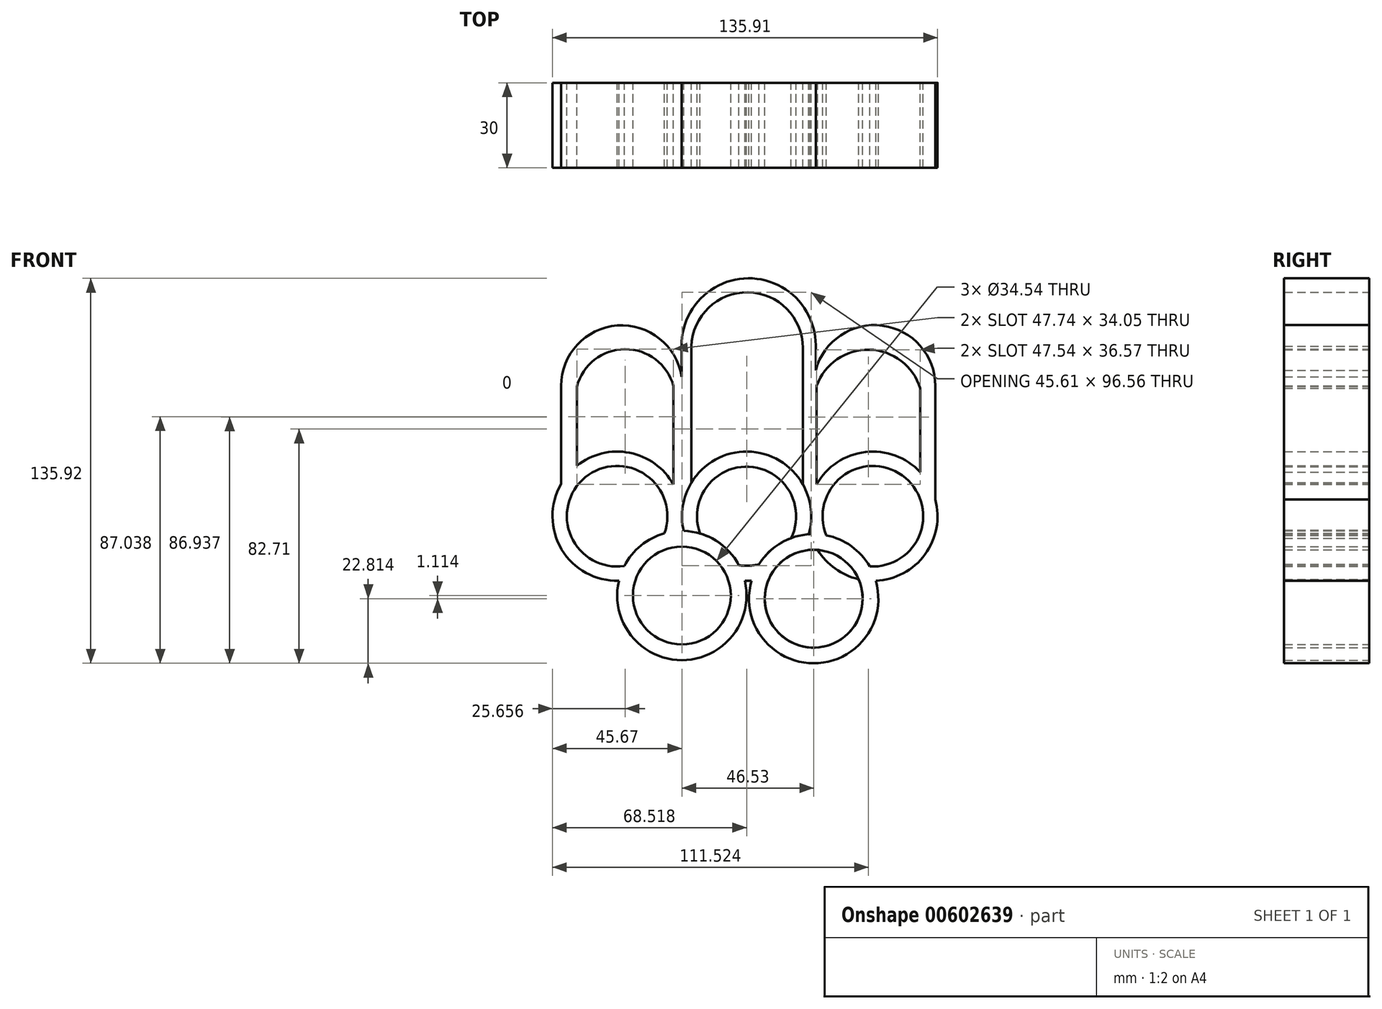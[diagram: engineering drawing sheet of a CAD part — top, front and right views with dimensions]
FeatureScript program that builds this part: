
annotation { "Feature Type Name" : "Feature", "Feature Type Description" : "" }
export const myFeature = defineFeature(function(context is Context, id is Id, definition is map)
    precondition{}
    {
        {
            var Q0;
            Q0=qCreatedBy(makeId("Front.planeOp"),FACE);
            var sketch = newSketch(context, id + "F0", { "sketchPlane" : qUnion([Q0])});
            skPoint(sketch, "E0.center.orphan", {"position": v(-38.59, 0) * mm});
            skArc(sketch, "E1", {"start": v(-45.07, -5.2) * mm, "mid": v(-81.71, 17.68) * mm, "end": v(-66.66, -22.8) * mm});
            skArc(sketch, "E2", {"start": v(0.32, -6.37) * mm, "mid": v(-20.99, 22.8) * mm, "end": v(-43.81, -5.2) * mm});
            skArc(sketch, "E3", {"start": v(3.52, -11.9) * mm, "mid": v(9.68, -18.54) * mm, "end": v(17.94, -22.25) * mm});
            skCircle(sketch, "E4", {"center": v(-44.44, -28) * mm, "radius": 22.82 * mm});
            skCircle(sketch, "E5", {"center": v(2.09, -29.12) * mm, "radius": 22.82 * mm});
            skArc(sketch, "E6", {"start": v(-50.6, -6.03) * mm, "mid": v(-78.5, 13.75) * mm, "end": v(-64.73, -17.56) * mm});
            skArc(sketch, "E7", {"start": v(21.85, -17.71) * mm, "mid": v(33.33, 14.42) * mm, "end": v(6.57, -6.74) * mm});
            skLineSegment(sketch, "E8", {"start": v(-47.43, 11.24) * mm, "end": v(-47.43, 45.98) * mm});
            skLineSegment(sketch, "E9", {"start": v(-41.1, 11.85) * mm, "end": v(-41.1, 60) * mm});
            skLineSegment(sketch, "E10", {"start": v(-1.73, 11.24) * mm, "end": v(-1.73, 59.38) * mm});
            skPoint(sketch, "E11.start.orphan", {"position": v(3.13, 11.24) * mm});
            skLineSegment(sketch, "E12", {"start": v(3.13, 11.24) * mm, "end": v(3.13, 45.98) * mm});
            skLineSegment(sketch, "E13", {"start": v(-87.07, 45.98) * mm, "end": v(-87.07, 11.36) * mm});
            skLineSegment(sketch, "E14", {"start": v(45.03, 45.98) * mm, "end": v(45.03, 5.9) * mm});
            skLineSegment(sketch, "E15", {"start": v(-81.48, 17.87) * mm, "end": v(-81.48, 45.81) * mm});
            skLineSegment(sketch, "E16", {"start": v(39.7, 15.53) * mm, "end": v(39.7, 45.14) * mm});
            skPoint(sketch, "E17.1.internal.orphan", {"position": v(-87.07, 53.58) * mm});
            skPoint(sketch, "E18.1.internal.orphan", {"position": v(-87.07, 49.2) * mm});
            skPoint(sketch, "E18.2.internal.orphan", {"position": v(-83.36, 53.58) * mm});
            skPoint(sketch, "E18.6.internal.orphan", {"position": v(-48.22, 53.58) * mm});
            skArc(sketch, "E19", {"start": v(-44.5, 49.2) * mm, "mid": v(-67.28, 67.33) * mm, "end": v(-87.07, 45.98) * mm});
            skArc(sketch, "E20", {"start": v(-47.43, 45.98) * mm, "mid": v(-64.52, 58.98) * mm, "end": v(-81.48, 45.81) * mm});
            skLineSegment(sketch, "E21", {"start": v(-44.5, 49.2) * mm, "end": v(-44.5, 60) * mm});
            skArc(sketch, "E22", {"start": v(45.03, 45.98) * mm, "mid": v(26.36, 67.28) * mm, "end": v(2.8, 51.56) * mm});
            skArc(sketch, "E23", {"start": v(39.7, 45.14) * mm, "mid": v(21.72, 58.78) * mm, "end": v(3.13, 45.98) * mm});
            skArc(sketch, "E24", {"start": v(-1.73, 59.38) * mm, "mid": v(-21.11, 79.06) * mm, "end": v(-41.1, 60) * mm});
            skLineSegment(sketch, "E25", {"start": v(2.8, 51.56) * mm, "end": v(2.8, 60.34) * mm});
            skArc(sketch, "E26", {"start": v(2.8, 60.34) * mm, "mid": v(-21.03, 84) * mm, "end": v(-44.5, 60) * mm});
            skCircle(sketch, "E27", {"center": v(-44.44, -28) * mm, "radius": 17.27 * mm});
            skCircle(sketch, "E28", {"center": v(2.09, -29.12) * mm, "radius": 17.27 * mm});
            skArc(sketch, "E29", {"start": v(-5.9, -7.74) * mm, "mid": v(-20.7, 17.48) * mm, "end": v(-38, -6.11) * mm});
            skArc(sketch, "E30.trimOffspring", {"start": v(24.01, -22.8) * mm, "mid": v(36.3, 18.54) * mm, "end": v(1.06, -6.32) * mm});
            skArc(sketch, "E31.trimOffspring", {"start": v(-22.22, -22.8) * mm, "mid": v(-21.02, -22.81) * mm, "end": v(-19.82, -22.75) * mm});
            skArc(sketch, "E32.trimOffspring", {"start": v(-24.3, -17.3) * mm, "mid": v(-20.73, -17.48) * mm, "end": v(-17.2, -16.94) * mm});
            skArc(sketch, "E33.trimOffspring", {"start": v(-41.6, -10.97) * mm, "mid": v(-36.02, -17.68) * mm, "end": v(-28.32, -21.8) * mm});
            skArc(sketch, "E34.trimOffspring", {"start": v(-60.56, -21.8) * mm, "mid": v(-52.86, -17.68) * mm, "end": v(-47.28, -10.97) * mm});
            skSolve(sketch);
        }
        {
            var Q0;
            Q0 = qSketchRegion(id + "F0", true);
            var Q1;
            {var subQ0=sQuery(id+"F0.wireOp",EDGE,"E6");var subQ1=sQuery(id+"F0.wireOp",EDGE,"E4");var subQ2=makeQuery(id+"F0.imprint","INTERSECT",VERTEX,{"disambiguationData":[OD(0.0)],"derivedFrom":[subQ1,subQ0]});Q1=makeQuery(id+"F0.imprint","IMPRINT",FACE,{"disambiguationData":[TD([[makeQuery(id+"F0.imprint","IMPRINT",EDGE,{"disambiguationData":[TD([[subQ2,-1.0]])],"derivedFrom":subQ1}),1.0]])]});}
            var Q2;
            {var subQ0=sQuery(id+"F0.wireOp",EDGE,"29F3q1Gk-59Qx-DLio-MAzj-wrFeAYEK7VN9");var subQ1=sQuery(id+"F0.wireOp",EDGE,"E1");var subQ2=makeQuery(id+"F0.imprint","INTERSECT",VERTEX,{"disambiguationData":[OD(0.0)],"derivedFrom":[subQ1,subQ0]});Q2=makeQuery(id+"F0.imprint","IMPRINT",FACE,{"disambiguationData":[TD([[makeQuery(id+"F0.imprint","IMPRINT",EDGE,{"disambiguationData":[TD([[subQ2,-1.0]])],"derivedFrom":subQ1}),1.0]])]});}
            var Q3;
            {var subQ0=sQuery(id+"F0.wireOp",EDGE,"29F3q1Gk-59Qx-DLio-MAzj-wrFeAYEK7VN9");var subQ1=sQuery(id+"F0.wireOp",EDGE,"E1");var subQ2=makeQuery(id+"F0.imprint","INTERSECT",VERTEX,{"disambiguationData":[OD(1.0)],"derivedFrom":[subQ1,subQ0]});Q3=makeQuery(id+"F0.imprint","IMPRINT",FACE,{"disambiguationData":[TD([[makeQuery(id+"F0.imprint","IMPRINT",EDGE,{"disambiguationData":[TD([[subQ2,-1.0]])],"derivedFrom":subQ1}),-1.0]])]});}
            var Q4;
            {var subQ0=sQuery(id+"F0.wireOp",EDGE,"29F3q1Gk-59Qx-DLio-MAzj-wrFeAYEK7VN9");var subQ1=sQuery(id+"F0.wireOp",EDGE,"E2");var subQ2=makeQuery(id+"F0.imprint","INTERSECT",VERTEX,{"disambiguationData":[OD(0.0)],"derivedFrom":[subQ1,subQ0]});Q4=makeQuery(id+"F0.imprint","IMPRINT",FACE,{"disambiguationData":[TD([[makeQuery(id+"F0.imprint","IMPRINT",EDGE,{"disambiguationData":[TD([[subQ2,-1.0]])],"derivedFrom":subQ1}),1.0]])]});}
            var Q5;
            {var subQ0=sQuery(id+"F0.wireOp",EDGE,"qcPD5Bay-Gsfa-sGTU-Rgtn-S3WhtxFdIdAI");var subQ1=sQuery(id+"F0.wireOp",EDGE,"E4");var subQ2=makeQuery(id+"F0.imprint","INTERSECT",VERTEX,{"disambiguationData":[OD(0.0)],"derivedFrom":[subQ1,subQ0]});Q5=makeQuery(id+"F0.imprint","IMPRINT",FACE,{"disambiguationData":[TD([[makeQuery(id+"F0.imprint","IMPRINT",EDGE,{"disambiguationData":[TD([[subQ2,-1.0]])],"derivedFrom":subQ1}),1.0]])]});}
            var Q6;
            {var subQ0=sQuery(id+"F0.wireOp",EDGE,"E2");var subQ4=makeQuery(id+"F0.imprint","INTERSECT",VERTEX,{"derivedFrom":[subQ0,sQuery(id+"F0.wireOp",EDGE,"E10")]});Q6=makeQuery(id+"F0.imprint","IMPRINT",FACE,{"disambiguationData":[TD([[makeQuery(id+"F0.imprint","IMPRINT",EDGE,{"disambiguationData":[TD([[subQ4,1.0]])],"derivedFrom":subQ0}),1.0]])]});}
            var Q7;
            {var subQ0=sQuery(id+"F0.wireOp",EDGE,"JeexFHJX-C1Pv-IVd9-wVUE-wp2mIqmijwAB");var subQ1=sQuery(id+"F0.wireOp",EDGE,"E2");var subQ2=makeQuery(id+"F0.imprint","INTERSECT",VERTEX,{"disambiguationData":[OD(0.0)],"derivedFrom":[subQ1,subQ0]});Q7=makeQuery(id+"F0.imprint","IMPRINT",FACE,{"disambiguationData":[TD([[makeQuery(id+"F0.imprint","IMPRINT",EDGE,{"disambiguationData":[TD([[subQ2,-1.0]])],"derivedFrom":subQ1}),1.0]])]});}
            var Q8;
            {var subQ0=sQuery(id+"F0.wireOp",EDGE,"qcPD5Bay-Gsfa-sGTU-Rgtn-S3WhtxFdIdAI");var subQ1=sQuery(id+"F0.wireOp",EDGE,"E5");var subQ2=makeQuery(id+"F0.imprint","INTERSECT",VERTEX,{"disambiguationData":[OD(0.0)],"derivedFrom":[subQ1,subQ0]});Q8=makeQuery(id+"F0.imprint","IMPRINT",FACE,{"disambiguationData":[TD([[makeQuery(id+"F0.imprint","IMPRINT",EDGE,{"disambiguationData":[TD([[subQ2,-1.0]])],"derivedFrom":subQ1}),1.0]])]});}
            var Q9;
            {var subQ0=sQuery(id+"F0.wireOp",EDGE,"E7");var subQ1=sQuery(id+"F0.wireOp",EDGE,"E5");var subQ2=makeQuery(id+"F0.imprint","INTERSECT",VERTEX,{"disambiguationData":[OD(0.0)],"derivedFrom":[subQ1,subQ0]});Q9=makeQuery(id+"F0.imprint","IMPRINT",FACE,{"disambiguationData":[TD([[makeQuery(id+"F0.imprint","IMPRINT",EDGE,{"disambiguationData":[TD([[subQ2,-1.0]])],"derivedFrom":subQ1}),1.0]])]});}
            var Q10;
            {var subQ0=sQuery(id+"F0.wireOp",EDGE,"JeexFHJX-C1Pv-IVd9-wVUE-wp2mIqmijwAB");var subQ1=sQuery(id+"F0.wireOp",EDGE,"E3");var subQ2=makeQuery(id+"F0.imprint","INTERSECT",VERTEX,{"disambiguationData":[OD(0.0)],"derivedFrom":[subQ1,subQ0]});Q10=makeQuery(id+"F0.imprint","IMPRINT",FACE,{"disambiguationData":[TD([[makeQuery(id+"F0.imprint","IMPRINT",EDGE,{"disambiguationData":[TD([[subQ2,-1.0]])],"derivedFrom":subQ1}),1.0]])]});}
            var Q11;
            {var subQ0=sQuery(id+"F0.wireOp",EDGE,"JeexFHJX-C1Pv-IVd9-wVUE-wp2mIqmijwAB");var subQ1=sQuery(id+"F0.wireOp",EDGE,"E2");var subQ2=makeQuery(id+"F0.imprint","INTERSECT",VERTEX,{"disambiguationData":[OD(1.0)],"derivedFrom":[subQ1,subQ0]});Q11=makeQuery(id+"F0.imprint","IMPRINT",FACE,{"disambiguationData":[TD([[makeQuery(id+"F0.imprint","IMPRINT",EDGE,{"disambiguationData":[TD([[subQ2,-1.0]])],"derivedFrom":subQ1}),-1.0]])]});}
            extrude(context, id + "F1", {"entities" : qUnion([Q0, Q1, Q2, Q3, Q4, Q5, Q6, Q7, Q8, Q9, Q10, Q11]), "depth" : 30 * mm, "offsetDistance" : 25 * mm});
        }
        {
            var Q0;
            Q0 = qSketchRegion(id + "F0", true);
            extrude(context, id + "F2", {"entities" : qUnion([Q0]), "depth" : 30 * mm, "offsetDistance" : 25 * mm});
        }
    });
